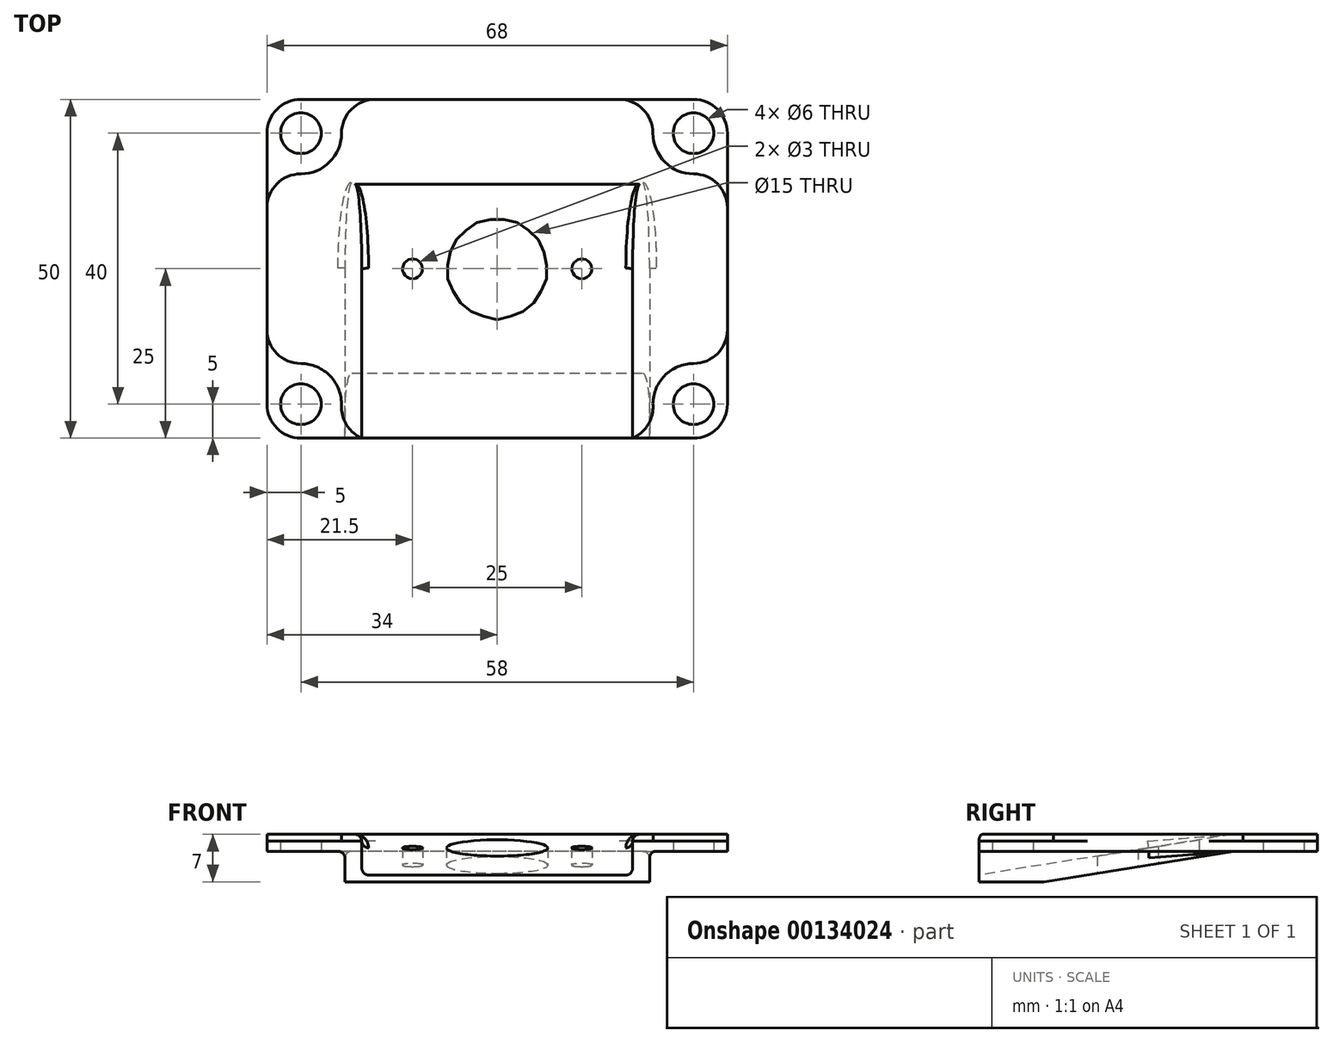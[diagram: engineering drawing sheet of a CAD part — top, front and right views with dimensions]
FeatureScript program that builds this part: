
annotation { "Feature Type Name" : "Feature", "Feature Type Description" : "" }
export const myFeature = defineFeature(function(context is Context, id is Id, definition is map)
    precondition{}
    {
        {
            var Q0;
            Q0=qCreatedBy(makeId("Right.planeOp"),FACE);
            var sketch = newSketch(context, id + "F0", { "sketchPlane" : qUnion([Q0])});
            skLineSegment(sketch, "E0", {"start": v(-25, 0) * mm, "end": v(25, 0) * mm});
            skLineSegment(sketch, "E1", {"start": v(25, 0) * mm, "end": v(25, 8) * mm});
            skLineSegment(sketch, "E2", {"start": v(-25, 8) * mm, "end": v(-25, 0) * mm});
            skLineSegment(sketch, "E3", {"start": v(25, 8) * mm, "end": v(-25, 8) * mm});
            skSolve(sketch);
        }
        {
            var Q0;
            Q0=makeQuery(id+"F0.imprint","IMPRINT",FACE,{"disambiguationData":[TD([[makeQuery(id+"F0.imprint","IMPRINT",EDGE,{"derivedFrom":sQuery(id+"F0.wireOp",EDGE,"E0")}),1.0]])]});
            extrude(context, id + "F1", {"entities" : qUnion([Q0]), "endBound" : BoundingType.SYMMETRIC, "depth" : 68 * mm, "offsetDistance" : 25 * mm});
        }
        {
            var Q0;
            Q0=qCreatedBy(makeId("Right.planeOp"),FACE);
            var sketch = newSketch(context, id + "F2", { "sketchPlane" : qUnion([Q0])});
            skLineSegment(sketch, "E4", {"start": v(25, 10) * mm, "end": v(-25, 2) * mm});
            skLineSegment(sketch, "E5", {"start": v(-25, 2) * mm, "end": v(-25, 14.14) * mm});
            skLineSegment(sketch, "E6", {"start": v(-25, 14.14) * mm, "end": v(25, 14.14) * mm});
            skLineSegment(sketch, "E7", {"start": v(25, 14.14) * mm, "end": v(25, 10) * mm});
            skSolve(sketch);
        }
        {
            var Q0;
            Q0=makeQuery(id+"F2.imprint","IMPRINT",FACE,{"disambiguationData":[TD([[makeQuery(id+"F2.imprint","IMPRINT",EDGE,{"derivedFrom":sQuery(id+"F2.wireOp",EDGE,"E4")}),-1.0]])]});
            extrude(context, id + "F3", {"entities" : qUnion([Q0]), "operationType" : NewBodyOperationType.REMOVE, "endBound" : BoundingType.SYMMETRIC, "oppositeDirection" : true, "depth" : 40 * mm, "offsetDistance" : 25 * mm});
        }
        {
            var Q0;
            Q0=makeQuery(id+"F1.opExtrude","SWEPT_FACE",FACE,{"disambiguationData":[OSD([sQuery(id+"F0.wireOp",EDGE,"E0")])]});
            var Q1;
            Q1=makeQuery(id+"F1.opExtrude","CAP_FACE",FACE,{"disambiguationData":[OSD([sQuery(id+"F0.wireOp",EDGE,"E0"),sQuery(id+"F0.wireOp",EDGE,"E1"),sQuery(id+"F0.wireOp",EDGE,"E2"),sQuery(id+"F0.wireOp",EDGE,"E3")])],"isStart":true});
            var Q2;
            Q2=makeQuery(id+"F1.opExtrude","CAP_FACE",FACE,{"disambiguationData":[OSD([sQuery(id+"F0.wireOp",EDGE,"E0"),sQuery(id+"F0.wireOp",EDGE,"E1"),sQuery(id+"F0.wireOp",EDGE,"E2"),sQuery(id+"F0.wireOp",EDGE,"E3")])],"isStart":false});
            var Q3;
            Q3=makeQuery(id+"F1.opExtrude","SWEPT_FACE",FACE,{"disambiguationData":[OSD([sQuery(id+"F0.wireOp",EDGE,"E2")])]});
            var Q4;
            Q4=makeQuery(id+"F1.opExtrude","SWEPT_FACE",FACE,{"disambiguationData":[OSD([sQuery(id+"F0.wireOp",EDGE,"E1")])]});
            shell(context, id + "F4", {"entities" : qUnion([Q0, Q1, Q2, Q3, Q4]), "thickness" : 2.5 * mm});
        }
        {
            var Q0;
            Q0=qCreatedBy(makeId("Top.planeOp"),FACE);
            var sketch = newSketch(context, id + "F5", { "sketchPlane" : qUnion([Q0])});
            skCircle(sketch, "E8", {"center": v(0, 0) * mm, "radius": 7.5 * mm});
            skCircle(sketch, "E9", {"center": v(-12.5, 0) * mm, "radius": 1.5 * mm});
            skCircle(sketch, "E10", {"center": v(12.5, 0) * mm, "radius": 1.5 * mm});
            skCircle(sketch, "E11", {"center": v(-29, 20) * mm, "radius": 3 * mm});
            skCircle(sketch, "E12", {"center": v(-29, -20) * mm, "radius": 3 * mm});
            skCircle(sketch, "E13", {"center": v(29, -20) * mm, "radius": 3 * mm});
            skCircle(sketch, "E14", {"center": v(29, 20) * mm, "radius": 3 * mm});
            skSolve(sketch);
        }
        {
            var Q0;
            Q0=qSketchRegion(id+"F5",true);
            extrude(context, id + "F6", {"entities" : qUnion([Q0]), "operationType" : NewBodyOperationType.REMOVE, "depth" : 25 * mm, "offsetDistance" : 25 * mm});
        }
        {
            var Q0;
            Q0=makeQuery(id+"F1.opExtrude","CAP_EDGE",EDGE,{"disambiguationData":[OSD([sQuery(id+"F0.wireOp",EDGE,"E2")])],"isStart":false});
            var Q1;
            Q1=makeQuery(id+"F1.opExtrude","CAP_EDGE",EDGE,{"disambiguationData":[OSD([sQuery(id+"F0.wireOp",EDGE,"E1")])],"isStart":false});
            var Q2;
            Q2=makeQuery(id+"F1.opExtrude","CAP_EDGE",EDGE,{"disambiguationData":[OSD([sQuery(id+"F0.wireOp",EDGE,"E2")])],"isStart":true});
            var Q3;
            Q3=makeQuery(id+"F1.opExtrude","CAP_EDGE",EDGE,{"disambiguationData":[OSD([sQuery(id+"F0.wireOp",EDGE,"E1")])],"isStart":true});
            fillet(context, id + "F7", {"entities" : qUnion([Q0, Q1, Q2, Q3]), "radius" : 5 * mm, "tangentPropagation" : true, "allowEdgeOverflow" : false});
        }
        {
            var Q0;
            Q0=makeQuery(id+"F3.boolean.opBoolean","INTERSECT",EDGE,{"derivedFrom":[makeQuery(id+"F1.opExtrude","SWEPT_FACE",FACE,{"disambiguationData":[OSD([sQuery(id+"F0.wireOp",EDGE,"E3")])]}),makeQuery(id+"F3.opExtrude","CAP_FACE",FACE,{"disambiguationData":[OSD([sQuery(id+"F2.wireOp",EDGE,"E4"),sQuery(id+"F2.wireOp",EDGE,"E5"),sQuery(id+"F2.wireOp",EDGE,"E6"),sQuery(id+"F2.wireOp",EDGE,"E7")])],"isStart":false})]});
            var Q1;
            Q1=makeQuery(id+"F3.boolean.opBoolean","INTERSECT",EDGE,{"derivedFrom":[makeQuery(id+"F1.opExtrude","SWEPT_FACE",FACE,{"disambiguationData":[OSD([sQuery(id+"F0.wireOp",EDGE,"E3")])]}),makeQuery(id+"F3.opExtrude","CAP_FACE",FACE,{"disambiguationData":[OSD([sQuery(id+"F2.wireOp",EDGE,"E4"),sQuery(id+"F2.wireOp",EDGE,"E5"),sQuery(id+"F2.wireOp",EDGE,"E6"),sQuery(id+"F2.wireOp",EDGE,"E7")])],"isStart":true})]});
            var Q2;
            {var subQ0=sQuery(id+"F2.wireOp",EDGE,"E4");Q2=makeQuery(id+"F4.opShell","OFFSET_EDGE",EDGE,{"disambiguationData":[OSD([subQ0]),TDD([makeQuery(id+"F3.boolean.opBoolean","COPY",EDGE,{"derivedFrom":makeQuery(id+"F3.opExtrude","CAP_EDGE",EDGE,{"disambiguationData":[OSD([subQ0])],"isStart":true})})])]});}
            var Q3;
            {var subQ0=sQuery(id+"F2.wireOp",EDGE,"E4");Q3=makeQuery(id+"F4.opShell","OFFSET_EDGE",EDGE,{"disambiguationData":[OSD([subQ0]),TDD([makeQuery(id+"F3.boolean.opBoolean","COPY",EDGE,{"derivedFrom":makeQuery(id+"F3.opExtrude","CAP_EDGE",EDGE,{"disambiguationData":[OSD([subQ0])],"isStart":false})})])]});}
            fillet(context, id + "F8", {"entities" : qUnion([Q0, Q1, Q2, Q3]), "radius" : 1 * mm, "tangentPropagation" : true, "allowEdgeOverflow" : false});
        }
        {
            var Q0;
            Q0=makeQuery(id+"F3.boolean.opBoolean","COPY",EDGE,{"derivedFrom":makeQuery(id+"F3.opExtrude","CAP_EDGE",EDGE,{"disambiguationData":[OSD([sQuery(id+"F2.wireOp",EDGE,"E4")])],"isStart":false})});
            var Q1;
            Q1=makeQuery(id+"F3.boolean.opBoolean","COPY",EDGE,{"derivedFrom":makeQuery(id+"F3.opExtrude","CAP_EDGE",EDGE,{"disambiguationData":[OSD([sQuery(id+"F2.wireOp",EDGE,"E4")])],"isStart":true})});
            var Q2;
            {var subQ0=sQuery(id+"F2.wireOp",EDGE,"E7");var subQ1=sQuery(id+"F2.wireOp",EDGE,"E6");var subQ2=sQuery(id+"F2.wireOp",EDGE,"E5");var subQ3=sQuery(id+"F2.wireOp",EDGE,"E4");var subQ4=sQuery(id+"F0.wireOp",EDGE,"E3");Q2=makeQuery(id+"F4.opShell","OFFSET_EDGE",EDGE,{"disambiguationData":[OSD([subQ4,subQ3,subQ2,subQ1,subQ0]),TDD([makeQuery(id+"F3.boolean.opBoolean","INTERSECT",EDGE,{"derivedFrom":[makeQuery(id+"F1.opExtrude","SWEPT_FACE",FACE,{"disambiguationData":[OSD([subQ4])]}),makeQuery(id+"F3.opExtrude","CAP_FACE",FACE,{"disambiguationData":[OSD([subQ3,subQ2,subQ1,subQ0])],"isStart":false})]})])]});}
            var Q3;
            {var subQ0=sQuery(id+"F2.wireOp",EDGE,"E7");var subQ1=sQuery(id+"F2.wireOp",EDGE,"E6");var subQ2=sQuery(id+"F2.wireOp",EDGE,"E5");var subQ3=sQuery(id+"F2.wireOp",EDGE,"E4");var subQ4=sQuery(id+"F0.wireOp",EDGE,"E3");Q3=makeQuery(id+"F4.opShell","OFFSET_EDGE",EDGE,{"disambiguationData":[OSD([subQ4,subQ3,subQ2,subQ1,subQ0]),TDD([makeQuery(id+"F3.boolean.opBoolean","INTERSECT",EDGE,{"derivedFrom":[makeQuery(id+"F1.opExtrude","SWEPT_FACE",FACE,{"disambiguationData":[OSD([subQ4])]}),makeQuery(id+"F3.opExtrude","CAP_FACE",FACE,{"disambiguationData":[OSD([subQ3,subQ2,subQ1,subQ0])],"isStart":true})]})])]});}
            fillet(context, id + "F9", {"entities" : qUnion([Q0, Q1, Q2, Q3]), "radius" : 1 * mm, "tangentPropagation" : true, "allowEdgeOverflow" : false});
        }
        {
            var Q0;
            Q0=qCreatedBy(makeId("Right.planeOp"),FACE);
            var sketch = newSketch(context, id + "F10", { "sketchPlane" : qUnion([Q0])});
            skLineSegment(sketch, "E15.bottom", {"start": v(-40, 0) * mm, "end": v(40, 0) * mm});
            skLineSegment(sketch, "E15.top", {"start": v(-40, 1) * mm, "end": v(40, 1) * mm});
            skLineSegment(sketch, "E15.left", {"start": v(-40, 0) * mm, "end": v(-40, 1) * mm});
            skLineSegment(sketch, "E15.right", {"start": v(40, 0) * mm, "end": v(40, 1) * mm});
            skSolve(sketch);
        }
        {
            var Q0;
            Q0=makeQuery(id+"F10.imprint","IMPRINT",FACE,{"disambiguationData":[TD([[makeQuery(id+"F10.imprint","IMPRINT",EDGE,{"derivedFrom":sQuery(id+"F10.wireOp",EDGE,"E15.bottom")}),1.0]])]});
            extrude(context, id + "F11", {"entities" : qUnion([Q0]), "operationType" : NewBodyOperationType.REMOVE, "endBound" : BoundingType.SYMMETRIC, "oppositeDirection" : true, "depth" : 200 * mm, "offsetDistance" : 25 * mm});
        }
        {
            var Q0;
            {var subQ0=sQuery(id+"F0.wireOp",EDGE,"E2");var subQ2=sQuery(id+"F0.wireOp",EDGE,"E3");var subQ3=sQuery(id+"F0.wireOp",EDGE,"E1");Q0=makeQuery(id+"F3.boolean.opBoolean","SPLIT",FACE,{"disambiguationData":[TD([makeQuery(id+"F1.opExtrude","CAP_FACE",FACE,{"disambiguationData":[OSD([sQuery(id+"F0.wireOp",EDGE,"E0"),subQ3,subQ0,subQ2])],"isStart":true})])],"derivedFrom":makeQuery(id+"F1.opExtrude","SWEPT_FACE",FACE,{"disambiguationData":[OSD([subQ2])]})});}
            var sketch = newSketch(context, id + "F12", { "sketchPlane" : qUnion([Q0])});
            skCircle(sketch, "E16", {"center": v(-29, -20) * mm, "radius": 6 * mm});
            skCircle(sketch, "E17", {"center": v(29, -20) * mm, "radius": 6 * mm});
            skCircle(sketch, "E18", {"center": v(29, 20) * mm, "radius": 6 * mm});
            skCircle(sketch, "E19", {"center": v(-29, 20) * mm, "radius": 6 * mm});
            skSolve(sketch);
        }
        {
            var Q0;
            Q0=qSketchRegion(id+"F12",true);
            extrude(context, id + "F13", {"entities" : qUnion([Q0]), "operationType" : NewBodyOperationType.REMOVE, "oppositeDirection" : true, "depth" : 1 * mm, "offsetDistance" : 25 * mm});
        }
        {
            var Q0;
            Q0=makeQuery(id+"F13.boolean.opBoolean","INTERSECT",EDGE,{"derivedFrom":[makeQuery(id+"F1.opExtrude","SWEPT_FACE",FACE,{"disambiguationData":[OSD([sQuery(id+"F0.wireOp",EDGE,"E2")])]}),makeQuery(id+"F13.opExtrude","SWEPT_FACE",FACE,{"disambiguationData":[OSD([sQuery(id+"F12.wireOp",EDGE,"E16")])]})]});
            var Q1;
            Q1=makeQuery(id+"F13.boolean.opBoolean","INTERSECT",EDGE,{"derivedFrom":[makeQuery(id+"F1.opExtrude","CAP_FACE",FACE,{"disambiguationData":[OSD([sQuery(id+"F0.wireOp",EDGE,"E0"),sQuery(id+"F0.wireOp",EDGE,"E1"),sQuery(id+"F0.wireOp",EDGE,"E2"),sQuery(id+"F0.wireOp",EDGE,"E3")])],"isStart":true}),makeQuery(id+"F13.opExtrude","SWEPT_FACE",FACE,{"disambiguationData":[OSD([sQuery(id+"F12.wireOp",EDGE,"E16")])]})]});
            var Q2;
            Q2=makeQuery(id+"F13.boolean.opBoolean","INTERSECT",EDGE,{"derivedFrom":[makeQuery(id+"F1.opExtrude","SWEPT_FACE",FACE,{"disambiguationData":[OSD([sQuery(id+"F0.wireOp",EDGE,"E2")])]}),makeQuery(id+"F13.opExtrude","SWEPT_FACE",FACE,{"disambiguationData":[OSD([sQuery(id+"F12.wireOp",EDGE,"E17")])]})]});
            var Q3;
            Q3=makeQuery(id+"F13.boolean.opBoolean","INTERSECT",EDGE,{"derivedFrom":[makeQuery(id+"F1.opExtrude","CAP_FACE",FACE,{"disambiguationData":[OSD([sQuery(id+"F0.wireOp",EDGE,"E0"),sQuery(id+"F0.wireOp",EDGE,"E1"),sQuery(id+"F0.wireOp",EDGE,"E2"),sQuery(id+"F0.wireOp",EDGE,"E3")])],"isStart":false}),makeQuery(id+"F13.opExtrude","SWEPT_FACE",FACE,{"disambiguationData":[OSD([sQuery(id+"F12.wireOp",EDGE,"E17")])]})]});
            var Q4;
            Q4=makeQuery(id+"F13.boolean.opBoolean","INTERSECT",EDGE,{"derivedFrom":[makeQuery(id+"F1.opExtrude","CAP_FACE",FACE,{"disambiguationData":[OSD([sQuery(id+"F0.wireOp",EDGE,"E0"),sQuery(id+"F0.wireOp",EDGE,"E1"),sQuery(id+"F0.wireOp",EDGE,"E2"),sQuery(id+"F0.wireOp",EDGE,"E3")])],"isStart":false}),makeQuery(id+"F13.opExtrude","SWEPT_FACE",FACE,{"disambiguationData":[OSD([sQuery(id+"F12.wireOp",EDGE,"E18")])]})]});
            var Q5;
            Q5=makeQuery(id+"F13.boolean.opBoolean","INTERSECT",EDGE,{"derivedFrom":[makeQuery(id+"F1.opExtrude","SWEPT_FACE",FACE,{"disambiguationData":[OSD([sQuery(id+"F0.wireOp",EDGE,"E1")])]}),makeQuery(id+"F13.opExtrude","SWEPT_FACE",FACE,{"disambiguationData":[OSD([sQuery(id+"F12.wireOp",EDGE,"E18")])]})]});
            var Q6;
            Q6=makeQuery(id+"F13.boolean.opBoolean","INTERSECT",EDGE,{"derivedFrom":[makeQuery(id+"F1.opExtrude","SWEPT_FACE",FACE,{"disambiguationData":[OSD([sQuery(id+"F0.wireOp",EDGE,"E1")])]}),makeQuery(id+"F13.opExtrude","SWEPT_FACE",FACE,{"disambiguationData":[OSD([sQuery(id+"F12.wireOp",EDGE,"E19")])]})]});
            var Q7;
            Q7=makeQuery(id+"F13.boolean.opBoolean","INTERSECT",EDGE,{"derivedFrom":[makeQuery(id+"F1.opExtrude","CAP_FACE",FACE,{"disambiguationData":[OSD([sQuery(id+"F0.wireOp",EDGE,"E0"),sQuery(id+"F0.wireOp",EDGE,"E1"),sQuery(id+"F0.wireOp",EDGE,"E2"),sQuery(id+"F0.wireOp",EDGE,"E3")])],"isStart":true}),makeQuery(id+"F13.opExtrude","SWEPT_FACE",FACE,{"disambiguationData":[OSD([sQuery(id+"F12.wireOp",EDGE,"E19")])]})]});
            fillet(context, id + "F14", {"entities" : qUnion([Q0, Q1, Q2, Q3, Q4, Q5, Q6, Q7]), "radius" : 5 * mm, "tangentPropagation" : true, "allowEdgeOverflow" : false});
        }
    });
